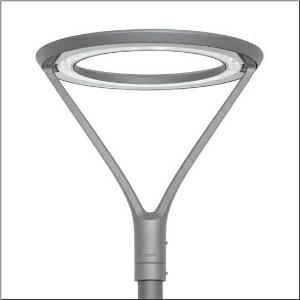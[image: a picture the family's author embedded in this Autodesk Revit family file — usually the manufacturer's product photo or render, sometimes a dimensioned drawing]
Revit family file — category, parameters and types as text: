
# Revit family: dl_r__20___pl1_2s_5xa51283ws008_843d
name_source: partatom
category: Lighting Fixtures
units: mm (PartAtom-declared; Revit-internal decimal feet)

## family parameters
Cut with Voids When Loaded = No
Host = Face
Light Source = No
Part Type = Normal
Room Calculation Point = No
Round Connector Dimension = Use Diameter
Shared = No

## types (1)
- --- (1 x LED, 3080 lm, 24.6 W, 3000K)
    Apparent Load = 25 VA
    CIE Flux Codes = 33 78 99 100 100
    Color Rendering = 70
    Color Temperature = 3000K
    Default Elevation = 1800 mm
    Description = DL® 20, mast luminaire, primary light control with reflector, highly specular, primary optical cover: cover, of toughened safety glass of clear glass with excellent transmission level, light distribution: PL1.2s, light emission: direct distribution, primary light characteristic: symmetric, installation type: post-top, LED, High Power LED, rated luminous flux: 3.040lm, luminous efficacy: 86lm/W, light colour: 730, colour temperature: 3000K, control gear: Plus, control: overheat protection, power reduction, digital communication interface, constant luminous flux control, time-dependent luminous flux control, flexible luminous flux parameterisation, electronic power reduction, mains connection: 230..240V, 50/60Hz, connection cable pre-assembled, cable length: 5m, start of lifetime: 36W, end of service life: 36W, reduction: 17W, luminaire housing, upper part, of cast aluminium, powder-coated, Siteco® metallic grey (DB 702S), diameter: 690mm, height: 690mm, spigot size: 76mm (post-top), mounting height: 4..6m, luminaire housing, of cast aluminium, powder-coated, Siteco® metallic grey (DB 702S), equipment: standard, protection rating (complete): IP66, insulation class (complete): insulation class II (safety insulation), certification: CE, ENEC, VDE, impact resistance: IK08, permissible operating ambient temperature: -25..+35°C, standard-compliant lighting for roads and squares, packaging unit: 1 piece

Light Distribution: PL1.2s
    Height = 690 mm
    Lamp = 1 x LED
    Lamp Light Flux = 3080 lm
    Lamp Power = 24.6 W
    Lamp count = 1
    Length = 690 mm
    Luminous efficacy = 125 lm/W
    Manufacturer = Siteco
    ModVariant = No
    Model = 5XA51283WS008
    Number of Poles = 1
    OnlyDefault = Yes
    Power Factor = 1
    Product Name = DL® 20 | PL1.2s
    Product group = mast luminaire | pylon top
    ProductGroupID = 6100
    Protection Class = Protection class II
    Protection Degree = IP 66
    RLX_Detail_Level = 1
    RLX_Emergency_Light_Flux = 0 lm
    RLX_Emergency_Type = 0
    RLX_Emergency_Type_DB = No
    RlxData = <blob elided: 205385 chars, md5=3c2efacc>
    Socket = socket
    Standby Power = 0 W
    System Light Flux = 3080 lm
    System Power = 25 W
    Type Comments = factory setting: luminous flux: 100 % | dim-lin: 254 | 330 mA
    Type Image = l_1006001.jpg
    URL = http://relux.com
    VarID = @adj_098457
    Voltage = 0 V
    Weight = 0.00 kg
    Width = 0 mm  [stored 0 ft]

note: [stored X ft] marks values corroborated as IEEE doubles in the binary element streams (Revit-internal decimal feet)

## geometry (parser evidence)
native form markers: Blend x4, Sweep x10
no freeform markers — native parametric forms only
